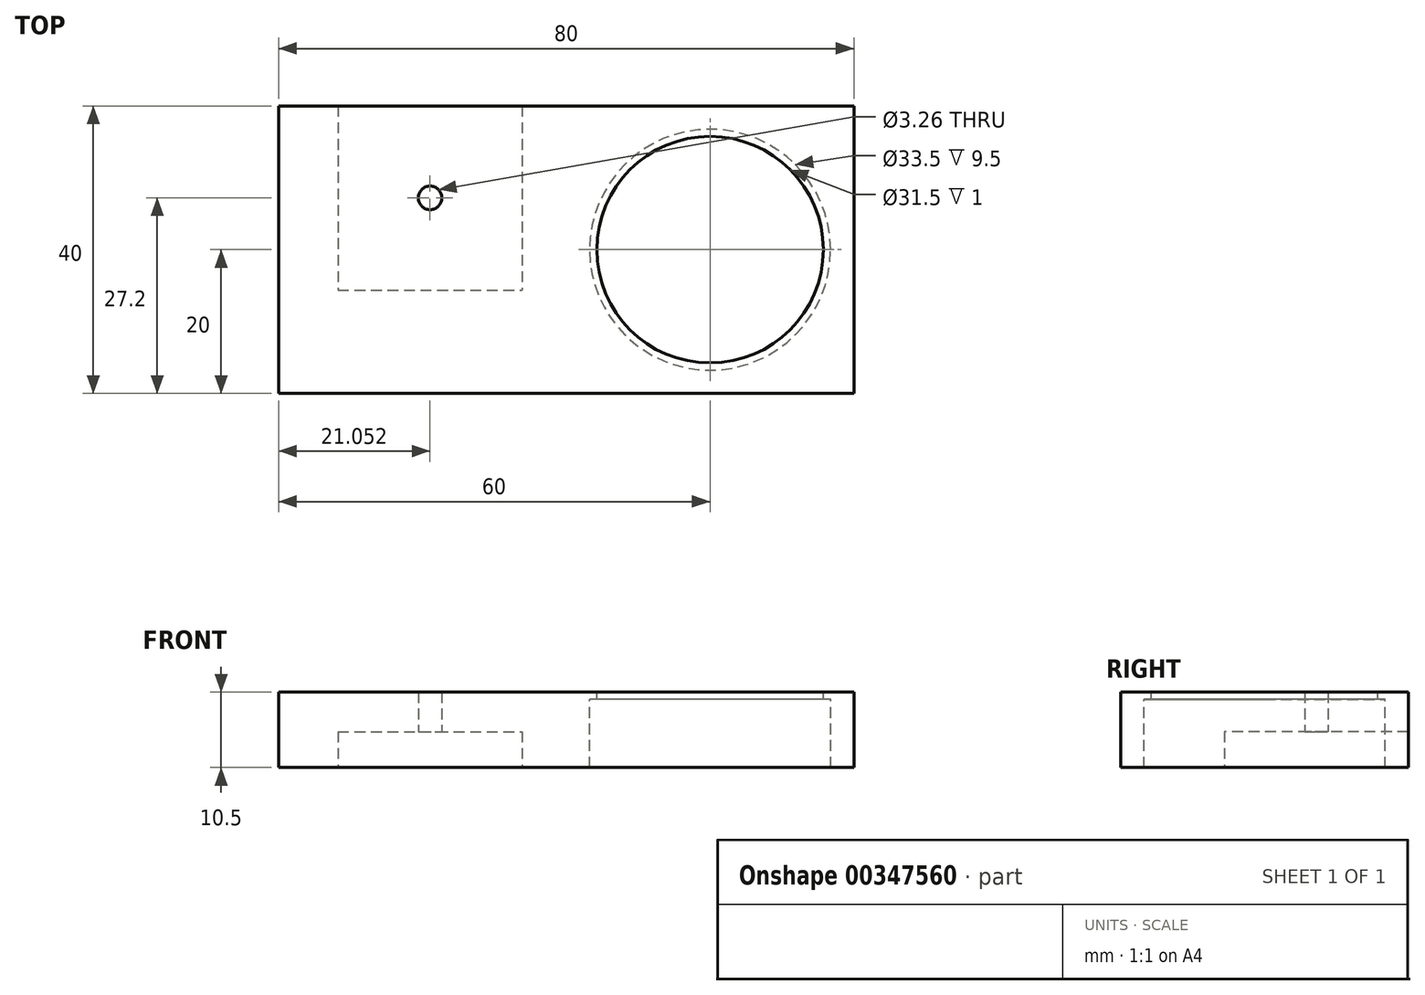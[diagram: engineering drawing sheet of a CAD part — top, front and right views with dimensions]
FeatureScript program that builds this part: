
annotation { "Feature Type Name" : "Feature", "Feature Type Description" : "" }
export const myFeature = defineFeature(function(context is Context, id is Id, definition is map)
    precondition{}
    {
        {
            var Q0;
            Q0=qCreatedBy(makeId("Top.planeOp"),FACE);
            var sketch = newSketch(context, id + "F0", { "sketchPlane" : qUnion([Q0])});
            skLineSegment(sketch, "E0.bottom", {"start": v(-40, 20) * mm, "end": v(40, 20) * mm});
            skLineSegment(sketch, "E0.top", {"start": v(-40, -20) * mm, "end": v(40, -20) * mm});
            skLineSegment(sketch, "E0.left", {"start": v(-40, 20) * mm, "end": v(-40, -20) * mm});
            skLineSegment(sketch, "E0.right", {"start": v(40, 20) * mm, "end": v(40, -20) * mm});
            skPoint(sketch, "E0.middle", {"position": v(0, 0) * mm});
            skSolve(sketch);
        }
        {
            var Q0;
            Q0=makeQuery(id+"F0.imprint","IMPRINT",FACE,{"disambiguationData":[TD([[makeQuery(id+"F0.imprint","IMPRINT",EDGE,{"derivedFrom":sQuery(id+"F0.wireOp",EDGE,"E0.bottom")}),-1.0]])]});
            extrude(context, id + "F1", {"entities" : qUnion([Q0]), "depth" : 9.5 * mm});
        }
        {
            var Q0;
            Q0=makeQuery(id+"F1.opExtrude","CAP_FACE",FACE,{"disambiguationData":[OSD([sQuery(id+"F0.wireOp",EDGE,"E0.bottom"),sQuery(id+"F0.wireOp",EDGE,"E0.top"),sQuery(id+"F0.wireOp",EDGE,"E0.left"),sQuery(id+"F0.wireOp",EDGE,"E0.right")])],"isStart":false});
            var sketch = newSketch(context, id + "F2", { "sketchPlane" : qUnion([Q0])});
            skCircle(sketch, "E1", {"center": v(20, 0) * mm, "radius": 16.75 * mm});
            skSolve(sketch);
        }
        {
            var Q0;
            Q0=makeQuery(id+"F2.imprint","IMPRINT",FACE,{"disambiguationData":[TD([[makeQuery(id+"F2.imprint","IMPRINT",EDGE,{"derivedFrom":sQuery(id+"F2.wireOp",EDGE,"E1")}),1.0]])]});
            extrude(context, id + "F3", {"entities" : qUnion([Q0]), "operationType" : NewBodyOperationType.REMOVE, "oppositeDirection" : true, "depth" : 9.5 * mm});
        }
        {
            var Q0;
            Q0=makeQuery(id+"F1.opExtrude","CAP_FACE",FACE,{"disambiguationData":[OSD([sQuery(id+"F0.wireOp",EDGE,"E0.bottom"),sQuery(id+"F0.wireOp",EDGE,"E0.top"),sQuery(id+"F0.wireOp",EDGE,"E0.left"),sQuery(id+"F0.wireOp",EDGE,"E0.right")])],"isStart":false});
            var sketch = newSketch(context, id + "F4", { "sketchPlane" : qUnion([Q0])});
            skLineSegment(sketch, "E2.bottom", {"start": v(40, 20) * mm, "end": v(-40, 20) * mm});
            skLineSegment(sketch, "E2.top", {"start": v(40, -20) * mm, "end": v(-40, -20) * mm});
            skLineSegment(sketch, "E2.left", {"start": v(40, 20) * mm, "end": v(40, -20) * mm});
            skLineSegment(sketch, "E2.right", {"start": v(-40, 20) * mm, "end": v(-40, -20) * mm});
            skPoint(sketch, "E2.middle", {"position": v(0, 0) * mm});
            skSolve(sketch);
        }
        {
            var Q0;
            Q0 = qSketchRegion(id + "F4", true);
            extrude(context, id + "F5", {"entities" : qUnion([Q0]), "operationType" : NewBodyOperationType.ADD, "depth" : 1 * mm});
        }
        {
            var Q0;
            Q0=makeQuery(id+"F5.opExtrude","CAP_FACE",FACE,{"disambiguationData":[OSD([sQuery(id+"F4.wireOp",EDGE,"E2.bottom"),sQuery(id+"F4.wireOp",EDGE,"E2.top"),sQuery(id+"F4.wireOp",EDGE,"E2.left"),sQuery(id+"F4.wireOp",EDGE,"E2.right")])],"isStart":false});
            var sketch = newSketch(context, id + "F6", { "sketchPlane" : qUnion([Q0])});
            skCircle(sketch, "E3", {"center": v(20, 0) * mm, "radius": 15.75 * mm});
            skSolve(sketch);
        }
        {
            var Q0;
            Q0=makeQuery(id+"F6.imprint","IMPRINT",FACE,{"disambiguationData":[TD([[makeQuery(id+"F6.imprint","IMPRINT",EDGE,{"derivedFrom":sQuery(id+"F6.wireOp",EDGE,"E3")}),1.0]])]});
            extrude(context, id + "F7", {"entities" : qUnion([Q0]), "operationType" : NewBodyOperationType.REMOVE, "oppositeDirection" : true, "depth" : 1 * mm});
        }
        {
            var Q0;
            Q0=makeQuery(id+"F1.opExtrude","CAP_FACE",FACE,{"disambiguationData":[OSD([sQuery(id+"F0.wireOp",EDGE,"E0.bottom"),sQuery(id+"F0.wireOp",EDGE,"E0.top"),sQuery(id+"F0.wireOp",EDGE,"E0.left"),sQuery(id+"F0.wireOp",EDGE,"E0.right")])],"isStart":true});
            var sketch = newSketch(context, id + "F8", { "sketchPlane" : qUnion([Q0])});
            skLineSegment(sketch, "E4.bottom", {"start": v(-31.75, -20) * mm, "end": v(-6.15, -20) * mm});
            skLineSegment(sketch, "E4.top", {"start": v(-31.75, 5.6) * mm, "end": v(-6.15, 5.6) * mm});
            skLineSegment(sketch, "E4.left", {"start": v(-31.75, -20) * mm, "end": v(-31.75, 5.6) * mm});
            skLineSegment(sketch, "E4.right", {"start": v(-6.15, -20) * mm, "end": v(-6.15, 5.6) * mm});
            skLineSegment(sketch, "E5", {"start": v(-18.95, 5.6) * mm, "end": v(-18.95, -20) * mm, "construction": true});
            skPoint(sketch, "E6", {"position": v(-18.95, -7.2) * mm});
            skSolve(sketch);
        }
        {
            var Q0;
            Q0=sQuery(id+"F8.wireOp",VERTEX,"E6");
            var Q1;
            Q1=makeQuery(id+"F1.opExtrude","SWEPT_BODY",BODY,{"disambiguationData":[OSD([sQuery(id+"F0.wireOp",EDGE,"E0.bottom"),sQuery(id+"F0.wireOp",EDGE,"E0.top"),sQuery(id+"F0.wireOp",EDGE,"E0.left"),sQuery(id+"F0.wireOp",EDGE,"E0.right")])]});
            hole(context, id + "F9", {"style" : HoleStyle.SIMPLE, "endStyle" : HoleEndStyle.THROUGH, "standardTappedOrClearance" : lookupTablePath({ "standard" : "ANSI", "fit" : "Normal (ASME)", "size" : "#4", "type" : "Clearance" }), "standardBlindInLast" : lookupTablePath({ "fit" : "Free", "standard" : "ANSI", "size" : "#4", "type" : "Clearance" }), "holeDiameter" : 3.26 * mm, "isTappedThrough" : true, "tappedDepth" : 12 * mm, "tapClearance" : 3, "startFromSketch" : true, "locations" : qUnion([Q0]), "scope" : qUnion([Q1])});
        }
        {
            var Q0;
            Q0=makeQuery(id+"F8.imprint","IMPRINT",FACE,{"disambiguationData":[TD([[makeQuery(id+"F8.imprint","IMPRINT",EDGE,{"derivedFrom":sQuery(id+"F8.wireOp",EDGE,"E4.bottom")}),1.0]])]});
            extrude(context, id + "F10", {"entities" : qUnion([Q0]), "operationType" : NewBodyOperationType.REMOVE, "oppositeDirection" : true, "depth" : 5 * mm});
        }
    });
